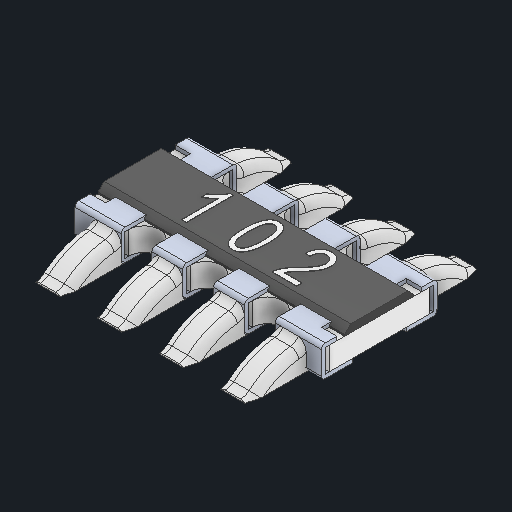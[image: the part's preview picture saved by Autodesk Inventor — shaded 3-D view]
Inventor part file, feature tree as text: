
AUTODESK INVENTOR PART (.ipt)
format: ipt  version: 2023 (Build 270158000, 158)  size: 518,144 bytes
history: native  units: in
note: dims shown in document units (in); Inventor stores cm internally (conversion verified against a paired STEP export)
features: other x8, fillet x2
ambient origin geometry x8: Origin, YZ Plane, XZ Plane, XY Plane, X Axis, Y Axis, Z Axis, Center Point
bodies: Solid1 (feature_tree), Solid2 (feature_tree), Solid3 (feature_tree), Solid4 (feature_tree), Solid5 (feature_tree), Solid6 (feature_tree), Solid7 (feature_tree), Solid8 (feature_tree), Solid9 (feature_tree), Solid10 (feature_tree)
feature tree (10):
  other  "Cut-Extrude7"
  other  "Boss-Extrude5"
  fillet  "Fillet2"  [1 undecoded]
  fillet  "Fillet1"  [1 undecoded]
  other  "LPattern3[1]"
  other  "LPattern3[2]"
  other  "LPattern3[3]"
  other  "LPattern3[4]"
  other  "LPattern3[5]"
  other  "LPattern3[6]"
note: 2 required parameter values undecoded (feature->parameter linkage not recoverable at this tier; creation-order binding heuristic only, values carry confidence <= 0.55)
